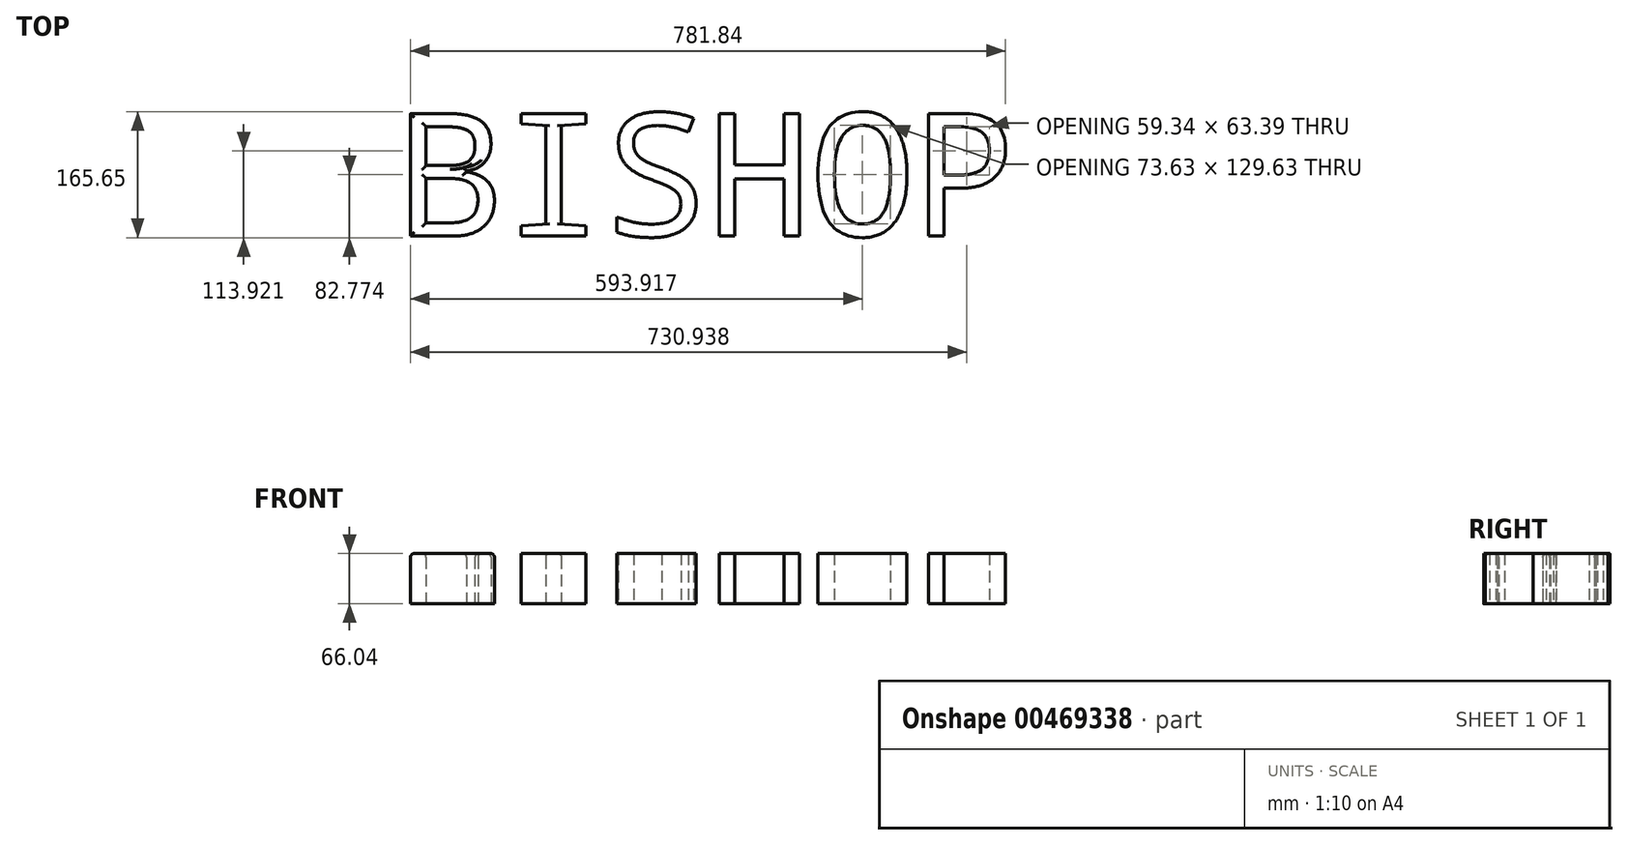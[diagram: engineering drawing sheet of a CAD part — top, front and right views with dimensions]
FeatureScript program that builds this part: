
annotation { "Feature Type Name" : "Feature", "Feature Type Description" : "" }
export const myFeature = defineFeature(function(context is Context, id is Id, definition is map)
    precondition{}
    {
        {
            var Q0;
            Q0=qCreatedBy(makeId("Top.planeOp"),FACE);
            var sketch = newSketch(context, id + "F0", { "sketchPlane" : qUnion([Q0])});
            skText(sketch, "E0", { "text": "BISHOP", "fontName": "DroidSansMono.ttf"});
            const initialGuessF0  = {"E0": [-0.17782, -0.09768, 1, 0, 0.16227]};
            skSetInitialGuess(sketch, initialGuessF0);
            skSolve(sketch);
        }
        {
            var Q0;
            Q0 = qSketchRegion(id + "F0", true);
            extrude(context, id + "F1", {"entities" : qUnion([Q0]), "depth" : 66.04 * mm});
        }
        {
            var Q0;
            Q0=makeQuery(id+"F1.opExtrude","CAP_EDGE",EDGE,{"disambiguationData":[OSD([sQuery(id+"F0.wireOp",EDGE,"E0.sketch_text.stroke-8")])],"isStart":false});
            var Q1;
            Q1=makeQuery(id+"F1.opExtrude","CAP_EDGE",EDGE,{"disambiguationData":[OSD([sQuery(id+"F0.wireOp",EDGE,"E0.sketch_text.stroke-21")])],"isStart":false});
            var Q2;
            Q2=makeQuery(id+"F1.opExtrude","CAP_EDGE",EDGE,{"disambiguationData":[OSD([sQuery(id+"F0.wireOp",EDGE,"E0.sketch_text.stroke-18")])],"isStart":false});
            var Q3;
            Q3=makeQuery(id+"F1.opExtrude","CAP_FACE",FACE,{"disambiguationData":[OSD([sQuery(id+"F0.wireOp",EDGE,"E0.sketch_text.stroke-0"),sQuery(id+"F0.wireOp",EDGE,"E0.sketch_text.stroke-1"),sQuery(id+"F0.wireOp",EDGE,"E0.sketch_text.stroke-2"),sQuery(id+"F0.wireOp",EDGE,"E0.sketch_text.stroke-3"),sQuery(id+"F0.wireOp",EDGE,"E0.sketch_text.stroke-4"),sQuery(id+"F0.wireOp",EDGE,"E0.sketch_text.stroke-5"),sQuery(id+"F0.wireOp",EDGE,"E0.sketch_text.stroke-6"),sQuery(id+"F0.wireOp",EDGE,"E0.sketch_text.stroke-7"),sQuery(id+"F0.wireOp",EDGE,"E0.sketch_text.stroke-8"),sQuery(id+"F0.wireOp",EDGE,"E0.sketch_text.stroke-9"),sQuery(id+"F0.wireOp",EDGE,"E0.sketch_text.stroke-10"),sQuery(id+"F0.wireOp",EDGE,"E0.sketch_text.stroke-11"),sQuery(id+"F0.wireOp",EDGE,"E0.sketch_text.stroke-12"),sQuery(id+"F0.wireOp",EDGE,"E0.sketch_text.stroke-13"),sQuery(id+"F0.wireOp",EDGE,"E0.sketch_text.stroke-14"),sQuery(id+"F0.wireOp",EDGE,"E0.sketch_text.stroke-15"),sQuery(id+"F0.wireOp",EDGE,"E0.sketch_text.stroke-16"),sQuery(id+"F0.wireOp",EDGE,"E0.sketch_text.stroke-17"),sQuery(id+"F0.wireOp",EDGE,"E0.sketch_text.stroke-18"),sQuery(id+"F0.wireOp",EDGE,"E0.sketch_text.stroke-19"),sQuery(id+"F0.wireOp",EDGE,"E0.sketch_text.stroke-20"),sQuery(id+"F0.wireOp",EDGE,"E0.sketch_text.stroke-21"),sQuery(id+"F0.wireOp",EDGE,"E0.sketch_text.stroke-22")])],"isStart":false});
            var Q4;
            Q4=makeQuery(id+"F1.opExtrude","CAP_EDGE",EDGE,{"disambiguationData":[OSD([sQuery(id+"F0.wireOp",EDGE,"E0.sketch_text.stroke-32")])],"isStart":false});
            var Q5;
            Q5=makeQuery(id+"F1.opExtrude","CAP_EDGE",EDGE,{"disambiguationData":[OSD([sQuery(id+"F0.wireOp",EDGE,"E0.sketch_text.stroke-26")])],"isStart":false});
            fillet(context, id + "F2", {"entities" : qUnion([Q0, Q1, Q2, Q3, Q4, Q5]), "radius" : 5.08 * mm, "tangentPropagation" : true, "allowEdgeOverflow" : false});
        }
    });
